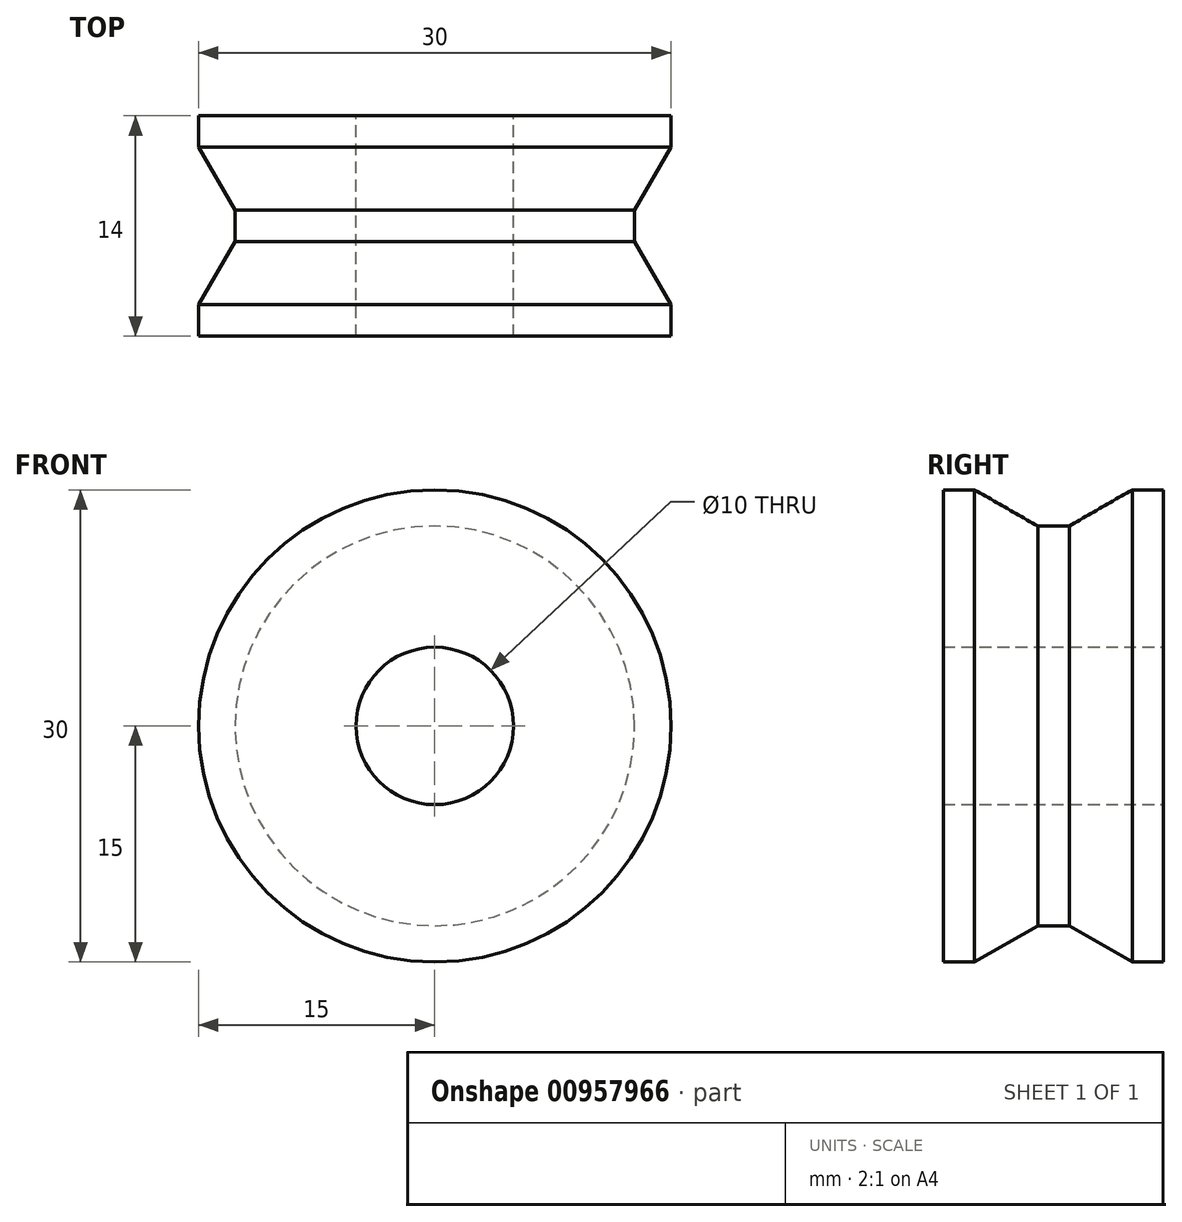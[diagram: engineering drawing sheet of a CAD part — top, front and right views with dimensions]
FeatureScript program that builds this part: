
annotation { "Feature Type Name" : "Feature", "Feature Type Description" : "" }
export const myFeature = defineFeature(function(context is Context, id is Id, definition is map)
    precondition{}
    {
        {
            var Q0;
            Q0=qCreatedBy(makeId("Top.planeOp"),FACE);
            var sketch = newSketch(context, id + "F0", { "sketchPlane" : qUnion([Q0])});
            skLineSegment(sketch, "E0", {"start": v(0, 0) * mm, "end": v(5, 0) * mm});
            skLineSegment(sketch, "E1", {"start": v(5, -7) * mm, "end": v(5, 7) * mm});
            skLineSegment(sketch, "E2", {"start": v(5, 7) * mm, "end": v(15, 7) * mm});
            skLineSegment(sketch, "E3", {"start": v(15, 7) * mm, "end": v(15, 5) * mm});
            skLineSegment(sketch, "E4", {"start": v(15, 5) * mm, "end": v(12.7, 1) * mm});
            skLineSegment(sketch, "E5", {"start": v(12.7, 1) * mm, "end": v(12.7, -1) * mm});
            skLineSegment(sketch, "E6", {"start": v(12.7, -1) * mm, "end": v(15, -5) * mm});
            skLineSegment(sketch, "E7", {"start": v(15, -5) * mm, "end": v(15, -7) * mm});
            skLineSegment(sketch, "E8", {"start": v(15, -7) * mm, "end": v(5, -7) * mm});
            skLineSegment(sketch, "E9", {"start": v(0, 6.04) * mm, "end": v(0, -6.04) * mm, "construction": true});
            skCircle(sketch, "E10", {"center": v(19.04, 0) * mm, "radius": 6 * mm, "construction": true});
            skSolve(sketch);
        }
        {
            var Q0;
            {var subQ0=sQuery(id+"F0.wireOp",EDGE,"E2");Q0=makeQuery(id+"F0.imprint","IMPRINT",FACE,{"disambiguationData":[TD([[makeQuery(id+"F0.imprint","IMPRINT",EDGE,{"derivedFrom":subQ0}),-1.0]])]});}
            var Q1;
            Q1=sQuery(id+"F0.wireOp",EDGE,"E2");
            var Q2;
            Q2=sQuery(id+"F0.wireOp",EDGE,"E3");
            var Q3;
            Q3=sQuery(id+"F0.wireOp",EDGE,"E4");
            var Q4;
            Q4=sQuery(id+"F0.wireOp",EDGE,"E5");
            var Q5;
            Q5=sQuery(id+"F0.wireOp",EDGE,"E6");
            var Q6;
            Q6=sQuery(id+"F0.wireOp",EDGE,"E7");
            var Q7;
            Q7=sQuery(id+"F0.wireOp",EDGE,"E8");
            var Q8;
            Q8=sQuery(id+"F0.wireOp",EDGE,"E1");
            var Q9;
            Q9=sQuery(id+"F0.wireOp",EDGE,"E9");
            revolve(context, id + "F1", {"surfaceOperationType" : NewSurfaceOperationType.NEW, "entities" : qUnion([Q0]), "surfaceEntities" : qUnion([Q1, Q2, Q3, Q4, Q5, Q6, Q7, Q8]), "axis" : qUnion([Q9]), "revolveType" : RevolveType.FULL});
        }
    });
